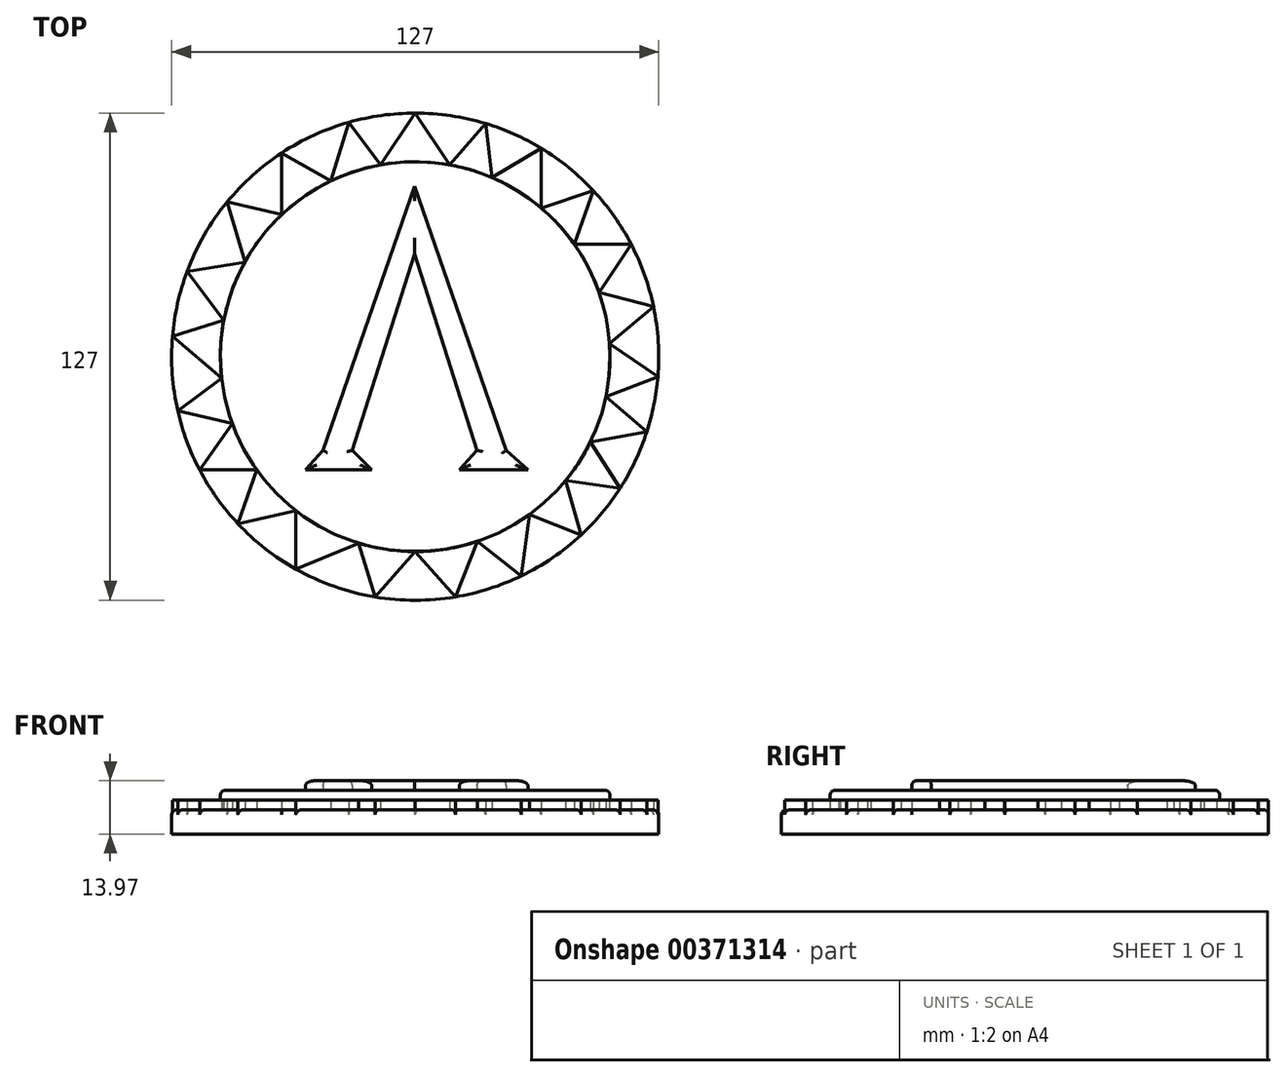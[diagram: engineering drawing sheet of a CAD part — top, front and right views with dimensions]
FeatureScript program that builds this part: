
annotation { "Feature Type Name" : "Feature", "Feature Type Description" : "" }
export const myFeature = defineFeature(function(context is Context, id is Id, definition is map)
    precondition{}
    {
        {
            var Q0;
            Q0=qCreatedBy(makeId("Top.planeOp"),FACE);
            var sketch = newSketch(context, id + "F0", { "sketchPlane" : qUnion([Q0])});
            skCircle(sketch, "E0", {"center": v(0, 0) * mm, "radius": 50.8 * mm});
            skCircle(sketch, "E1", {"center": v(0, 0) * mm, "radius": 63.5 * mm});
            skPoint(sketch, "E2", {"position": v(9.04, 49.99) * mm});
            skPoint(sketch, "E3", {"position": v(-9.05, 49.99) * mm});
            skLineSegment(sketch, "E4", {"start": v(9.04, 49.99) * mm, "end": v(18.33, 60.8) * mm});
            skLineSegment(sketch, "E5", {"start": v(18.33, 60.8) * mm, "end": v(19.99, 46.7) * mm});
            skLineSegment(sketch, "E6", {"start": v(19.99, 46.7) * mm, "end": v(32.82, 54.36) * mm});
            skLineSegment(sketch, "E7", {"start": v(32.82, 54.36) * mm, "end": v(32.82, 38.78) * mm});
            skLineSegment(sketch, "E8", {"start": v(32.82, 38.78) * mm, "end": v(46.5, 43.25) * mm});
            skLineSegment(sketch, "E9", {"start": v(46.5, 43.25) * mm, "end": v(41.51, 29.28) * mm});
            skLineSegment(sketch, "E10", {"start": v(41.51, 29.28) * mm, "end": v(56.35, 29.28) * mm});
            skLineSegment(sketch, "E11", {"start": v(56.35, 29.28) * mm, "end": v(47.98, 16.7) * mm});
            skLineSegment(sketch, "E12", {"start": v(47.98, 16.7) * mm, "end": v(62.14, 13.06) * mm});
            skLineSegment(sketch, "E13", {"start": v(62.14, 13.06) * mm, "end": v(50.69, 3.39) * mm});
            skLineSegment(sketch, "E14", {"start": v(50.69, 3.39) * mm, "end": v(63.28, -5.26) * mm});
            skLineSegment(sketch, "E15", {"start": v(63.28, -5.26) * mm, "end": v(49.7, -10.49) * mm});
            skLineSegment(sketch, "E16", {"start": v(-9.05, 49.99) * mm, "end": v(-17.31, 61.1) * mm});
            skLineSegment(sketch, "E17", {"start": v(-17.31, 61.1) * mm, "end": v(-22.05, 45.77) * mm});
            skLineSegment(sketch, "E18", {"start": v(-22.05, 45.77) * mm, "end": v(-34.79, 53.12) * mm});
            skLineSegment(sketch, "E19", {"start": v(0, 63.5) * mm, "end": v(-9.05, 49.99) * mm});
            skLineSegment(sketch, "E20", {"start": v(0, 63.5) * mm, "end": v(9.04, 49.99) * mm});
            skLineSegment(sketch, "E21", {"start": v(-34.79, 53.12) * mm, "end": v(-34.79, 37.02) * mm});
            skLineSegment(sketch, "E22", {"start": v(-34.79, 37.02) * mm, "end": v(-49.02, 40.36) * mm});
            skLineSegment(sketch, "E23", {"start": v(-49.02, 40.36) * mm, "end": v(-44.42, 24.65) * mm});
            skLineSegment(sketch, "E24", {"start": v(-44.42, 24.65) * mm, "end": v(-59.47, 22.26) * mm});
            skLineSegment(sketch, "E25", {"start": v(-59.47, 22.26) * mm, "end": v(-49.9, 9.5) * mm});
            skLineSegment(sketch, "E26", {"start": v(-49.9, 9.5) * mm, "end": v(-63.28, 5.27) * mm});
            skLineSegment(sketch, "E27", {"start": v(-63.28, 5.27) * mm, "end": v(-50.49, -5.64) * mm});
            skLineSegment(sketch, "E28", {"start": v(-50.49, -5.64) * mm, "end": v(-61.91, -14.1) * mm});
            skLineSegment(sketch, "E29", {"start": v(-61.91, -14.1) * mm, "end": v(-47.71, -17.44) * mm});
            skLineSegment(sketch, "E30", {"start": v(-47.71, -17.44) * mm, "end": v(-56.21, -29.54) * mm});
            skLineSegment(sketch, "E31", {"start": v(-56.21, -29.54) * mm, "end": v(-41.33, -29.54) * mm});
            skLineSegment(sketch, "E32", {"start": v(-41.33, -29.54) * mm, "end": v(-46.22, -43.55) * mm});
            skLineSegment(sketch, "E33", {"start": v(-46.22, -43.55) * mm, "end": v(-31.1, -40.17) * mm});
            skLineSegment(sketch, "E34", {"start": v(-31.1, -40.17) * mm, "end": v(-31.1, -55.36) * mm});
            skLineSegment(sketch, "E35", {"start": v(-31.1, -55.36) * mm, "end": v(-14.78, -48.6) * mm});
            skLineSegment(sketch, "E36", {"start": v(-14.78, -48.6) * mm, "end": v(-10.47, -62.63) * mm});
            skLineSegment(sketch, "E37", {"start": v(-10.47, -62.63) * mm, "end": v(0, -50.8) * mm});
            skLineSegment(sketch, "E38", {"start": v(0, -50.8) * mm, "end": v(10.47, -62.63) * mm});
            skLineSegment(sketch, "E39", {"start": v(10.47, -62.63) * mm, "end": v(16.28, -48.12) * mm});
            skLineSegment(sketch, "E40", {"start": v(16.28, -48.12) * mm, "end": v(27.67, -57.15) * mm});
            skLineSegment(sketch, "E41", {"start": v(27.67, -57.15) * mm, "end": v(29.84, -41.1) * mm});
            skLineSegment(sketch, "E42", {"start": v(29.84, -41.1) * mm, "end": v(43.26, -46.48) * mm});
            skLineSegment(sketch, "E43", {"start": v(43.26, -46.48) * mm, "end": v(39.22, -32.29) * mm});
            skLineSegment(sketch, "E44", {"start": v(39.22, -32.29) * mm, "end": v(53.46, -34.27) * mm});
            skLineSegment(sketch, "E45", {"start": v(53.46, -34.27) * mm, "end": v(45.69, -22.2) * mm});
            skLineSegment(sketch, "E46", {"start": v(49.7, -10.49) * mm, "end": v(60.42, -19.54) * mm});
            skLineSegment(sketch, "E47", {"start": v(45.69, -22.2) * mm, "end": v(60.42, -19.54) * mm});
            skPoint(sketch, "E48", {"position": v(0, 43.48) * mm});
            skPoint(sketch, "E49", {"position": v(0, -25.4) * mm});
            skPoint(sketch, "E50", {"position": v(0, 25.83) * mm});
            skLineSegment(sketch, "E51", {"start": v(0, 25.83) * mm, "end": v(16.25, -25.4) * mm});
            skLineSegment(sketch, "E52", {"start": v(0, 25.83) * mm, "end": v(-16.25, -25.4) * mm});
            skLineSegment(sketch, "E53", {"start": v(0, 43.48) * mm, "end": v(-23.87, -25.4) * mm});
            skLineSegment(sketch, "E54", {"start": v(0, 43.48) * mm, "end": v(23.87, -25.4) * mm});
            skPoint(sketch, "E55", {"position": v(0, -30.48) * mm});
            skLineSegment(sketch, "E56", {"start": v(-23.87, -25.4) * mm, "end": v(-28.47, -30.48) * mm});
            skLineSegment(sketch, "E57", {"start": v(-16.25, -25.4) * mm, "end": v(-11.25, -30.48) * mm});
            skLineSegment(sketch, "E58", {"start": v(16.25, -25.4) * mm, "end": v(11.66, -30.48) * mm});
            skLineSegment(sketch, "E59", {"start": v(23.87, -25.4) * mm, "end": v(29.5, -30.48) * mm});
            skLineSegment(sketch, "E60", {"start": v(-11.25, -30.48) * mm, "end": v(-28.47, -30.48) * mm});
            skLineSegment(sketch, "E61", {"start": v(11.66, -30.48) * mm, "end": v(29.5, -30.48) * mm});
            skPoint(sketch, "E62", {"position": v(0, 50.8) * mm});
            skLineSegment(sketch, "E63", {"start": v(0, 0) * mm, "end": v(-8.2, 0) * mm});
            skLineSegment(sketch, "E64", {"start": v(0, 0) * mm, "end": v(8.2, 0) * mm});
            skSolve(sketch);
        }
        {
            var Q0;
            Q0 = qSketchRegion(id + "F0", true);
            var Q1;
            Q1=makeQuery(id+"F0.imprint","IMPRINT",FACE,{"disambiguationData":[TD([[makeQuery(id+"F0.imprint","IMPRINT",EDGE,{"derivedFrom":sQuery(id+"F0.wireOp",EDGE,"E51")}),-1.0]])]});
            var Q2;
            Q2=makeQuery(id+"F0.imprint","IMPRINT",FACE,{"disambiguationData":[TD([[makeQuery(id+"F0.imprint","IMPRINT",EDGE,{"derivedFrom":sQuery(id+"F0.wireOp",EDGE,"E51")}),1.0]])]});
            var Q3;
            Q3=makeQuery(id+"F0.imprint","IMPRINT",FACE,{"disambiguationData":[TD([[makeQuery(id+"F0.imprint","IMPRINT",EDGE,{"derivedFrom":sQuery(id+"F0.wireOp",EDGE,"E53")}),-1.0]])]});
            extrude(context, id + "F1", {"entities" : qUnion([Q0, Q1, Q2, Q3]), "depth" : 6.35 * mm});
        }
        {
            var Q0;
            Q0=makeQuery(id+"F1.opExtrude","CAP_FACE",FACE,{"disambiguationData":[OSD([sQuery(id+"F0.wireOp",EDGE,"E0"),sQuery(id+"F0.wireOp",EDGE,"E1")])],"isStart":false});
            var sketch = newSketch(context, id + "F2", { "sketchPlane" : qUnion([Q0])});
            skCircle(sketch, "E65", {"center": v(0, 0) * mm, "radius": 63.5 * mm});
            skPoint(sketch, "E66", {"position": v(9.04, 49.99) * mm});
            skPoint(sketch, "E67", {"position": v(-9.05, 49.99) * mm});
            skLineSegment(sketch, "E68", {"start": v(9.04, 49.99) * mm, "end": v(18.33, 60.8) * mm});
            skLineSegment(sketch, "E69", {"start": v(18.33, 60.8) * mm, "end": v(19.99, 46.7) * mm});
            skLineSegment(sketch, "E70", {"start": v(19.99, 46.7) * mm, "end": v(32.82, 54.36) * mm});
            skLineSegment(sketch, "E71", {"start": v(32.82, 54.36) * mm, "end": v(32.82, 38.78) * mm});
            skLineSegment(sketch, "E72", {"start": v(32.82, 38.78) * mm, "end": v(46.5, 43.25) * mm});
            skLineSegment(sketch, "E73", {"start": v(46.5, 43.25) * mm, "end": v(41.51, 29.28) * mm});
            skLineSegment(sketch, "E74", {"start": v(41.51, 29.28) * mm, "end": v(56.35, 29.28) * mm});
            skLineSegment(sketch, "E75", {"start": v(56.35, 29.28) * mm, "end": v(47.98, 16.7) * mm});
            skLineSegment(sketch, "E76", {"start": v(47.98, 16.7) * mm, "end": v(62.14, 13.06) * mm});
            skLineSegment(sketch, "E77", {"start": v(62.14, 13.06) * mm, "end": v(50.69, 3.39) * mm});
            skLineSegment(sketch, "E78", {"start": v(50.69, 3.39) * mm, "end": v(63.28, -5.26) * mm});
            skLineSegment(sketch, "E79", {"start": v(63.28, -5.26) * mm, "end": v(49.7, -10.49) * mm});
            skLineSegment(sketch, "E80", {"start": v(-9.05, 49.99) * mm, "end": v(-17.31, 61.1) * mm});
            skLineSegment(sketch, "E81", {"start": v(-17.31, 61.1) * mm, "end": v(-22.05, 45.77) * mm});
            skLineSegment(sketch, "E82", {"start": v(-22.05, 45.77) * mm, "end": v(-34.79, 53.12) * mm});
            skLineSegment(sketch, "E83", {"start": v(0, 63.5) * mm, "end": v(-9.05, 49.99) * mm});
            skLineSegment(sketch, "E84", {"start": v(0, 63.5) * mm, "end": v(9.04, 49.99) * mm});
            skLineSegment(sketch, "E85", {"start": v(-34.79, 53.12) * mm, "end": v(-34.79, 37.02) * mm});
            skLineSegment(sketch, "E86", {"start": v(-34.79, 37.02) * mm, "end": v(-49.02, 40.36) * mm});
            skLineSegment(sketch, "E87", {"start": v(-49.02, 40.36) * mm, "end": v(-44.42, 24.65) * mm});
            skLineSegment(sketch, "E88", {"start": v(-44.42, 24.65) * mm, "end": v(-59.47, 22.26) * mm});
            skLineSegment(sketch, "E89", {"start": v(-59.47, 22.26) * mm, "end": v(-49.9, 9.5) * mm});
            skLineSegment(sketch, "E90", {"start": v(-49.9, 9.5) * mm, "end": v(-63.28, 5.27) * mm});
            skLineSegment(sketch, "E91", {"start": v(-63.28, 5.27) * mm, "end": v(-50.49, -5.64) * mm});
            skLineSegment(sketch, "E92", {"start": v(-50.49, -5.64) * mm, "end": v(-61.91, -14.1) * mm});
            skLineSegment(sketch, "E93", {"start": v(-61.91, -14.1) * mm, "end": v(-47.71, -17.44) * mm});
            skLineSegment(sketch, "E94", {"start": v(-47.71, -17.44) * mm, "end": v(-56.21, -29.54) * mm});
            skLineSegment(sketch, "E95", {"start": v(-56.21, -29.54) * mm, "end": v(-41.33, -29.54) * mm});
            skLineSegment(sketch, "E96", {"start": v(-41.33, -29.54) * mm, "end": v(-46.22, -43.55) * mm});
            skLineSegment(sketch, "E97", {"start": v(-46.22, -43.55) * mm, "end": v(-31.1, -40.17) * mm});
            skLineSegment(sketch, "E98", {"start": v(-31.1, -40.17) * mm, "end": v(-31.1, -55.36) * mm});
            skLineSegment(sketch, "E99", {"start": v(-31.1, -55.36) * mm, "end": v(-14.78, -48.6) * mm});
            skLineSegment(sketch, "E100", {"start": v(-14.78, -48.6) * mm, "end": v(-10.47, -62.63) * mm});
            skLineSegment(sketch, "E101", {"start": v(-10.47, -62.63) * mm, "end": v(0, -50.8) * mm});
            skLineSegment(sketch, "E102", {"start": v(0, -50.8) * mm, "end": v(10.47, -62.63) * mm});
            skLineSegment(sketch, "E103", {"start": v(10.47, -62.63) * mm, "end": v(16.28, -48.12) * mm});
            skLineSegment(sketch, "E104", {"start": v(16.28, -48.12) * mm, "end": v(27.67, -57.15) * mm});
            skLineSegment(sketch, "E105", {"start": v(27.67, -57.15) * mm, "end": v(29.84, -41.1) * mm});
            skLineSegment(sketch, "E106", {"start": v(29.84, -41.1) * mm, "end": v(43.26, -46.48) * mm});
            skLineSegment(sketch, "E107", {"start": v(43.26, -46.48) * mm, "end": v(39.22, -32.29) * mm});
            skLineSegment(sketch, "E108", {"start": v(39.22, -32.29) * mm, "end": v(53.46, -34.27) * mm});
            skLineSegment(sketch, "E109", {"start": v(53.46, -34.27) * mm, "end": v(45.69, -22.2) * mm});
            skLineSegment(sketch, "E110", {"start": v(49.7, -10.49) * mm, "end": v(60.42, -19.54) * mm});
            skLineSegment(sketch, "E111", {"start": v(45.69, -22.2) * mm, "end": v(60.42, -19.54) * mm});
            skPoint(sketch, "E112", {"position": v(-74.35, 61.13) * mm});
            skPoint(sketch, "E113", {"position": v(-74.35, -7.75) * mm});
            skPoint(sketch, "E114", {"position": v(-74.35, 43.48) * mm});
            skPoint(sketch, "E115", {"position": v(-74.35, -12.83) * mm});
            skSolve(sketch);
        }
        {
            var Q0;
            Q0=makeQuery(id+"F2.imprint","IMPRINT",FACE,{"disambiguationData":[TD([[makeQuery(id+"F2.imprint","IMPRINT",EDGE,{"derivedFrom":sQuery(id+"F2.wireOp",EDGE,"E68")}),-1.0]])]});
            extrude(context, id + "F3", {"entities" : qUnion([Q0]), "operationType" : NewBodyOperationType.ADD, "depth" : 2.54 * mm});
        }
        {
            var Q0;
            Q0=makeQuery(id+"F3.opExtrude","CAP_FACE",FACE,{"disambiguationData":[OSD([sQuery(id+"F2.wireOp",EDGE,"E68"),sQuery(id+"F2.wireOp",EDGE,"E69"),sQuery(id+"F2.wireOp",EDGE,"E70"),sQuery(id+"F2.wireOp",EDGE,"E71"),sQuery(id+"F2.wireOp",EDGE,"E72"),sQuery(id+"F2.wireOp",EDGE,"E73"),sQuery(id+"F2.wireOp",EDGE,"E74"),sQuery(id+"F2.wireOp",EDGE,"E75"),sQuery(id+"F2.wireOp",EDGE,"E76"),sQuery(id+"F2.wireOp",EDGE,"E77"),sQuery(id+"F2.wireOp",EDGE,"E78"),sQuery(id+"F2.wireOp",EDGE,"E79"),sQuery(id+"F2.wireOp",EDGE,"E80"),sQuery(id+"F2.wireOp",EDGE,"E81"),sQuery(id+"F2.wireOp",EDGE,"E82"),sQuery(id+"F2.wireOp",EDGE,"E83"),sQuery(id+"F2.wireOp",EDGE,"E84"),sQuery(id+"F2.wireOp",EDGE,"E85"),sQuery(id+"F2.wireOp",EDGE,"E86"),sQuery(id+"F2.wireOp",EDGE,"E87"),sQuery(id+"F2.wireOp",EDGE,"E88"),sQuery(id+"F2.wireOp",EDGE,"E89"),sQuery(id+"F2.wireOp",EDGE,"E90"),sQuery(id+"F2.wireOp",EDGE,"E91"),sQuery(id+"F2.wireOp",EDGE,"E92"),sQuery(id+"F2.wireOp",EDGE,"E93"),sQuery(id+"F2.wireOp",EDGE,"E94"),sQuery(id+"F2.wireOp",EDGE,"E95"),sQuery(id+"F2.wireOp",EDGE,"E96"),sQuery(id+"F2.wireOp",EDGE,"E97"),sQuery(id+"F2.wireOp",EDGE,"E98"),sQuery(id+"F2.wireOp",EDGE,"E99"),sQuery(id+"F2.wireOp",EDGE,"E100"),sQuery(id+"F2.wireOp",EDGE,"E101"),sQuery(id+"F2.wireOp",EDGE,"E102"),sQuery(id+"F2.wireOp",EDGE,"E103"),sQuery(id+"F2.wireOp",EDGE,"E104"),sQuery(id+"F2.wireOp",EDGE,"E105"),sQuery(id+"F2.wireOp",EDGE,"E106"),sQuery(id+"F2.wireOp",EDGE,"E107"),sQuery(id+"F2.wireOp",EDGE,"E108"),sQuery(id+"F2.wireOp",EDGE,"E109"),sQuery(id+"F2.wireOp",EDGE,"E110"),sQuery(id+"F2.wireOp",EDGE,"E111")])],"isStart":false});
            var sketch = newSketch(context, id + "F4", { "sketchPlane" : qUnion([Q0])});
            skPoint(sketch, "E116", {"position": v(0, 0) * mm});
            skCircle(sketch, "E117", {"center": v(0, 0) * mm, "radius": 50.8 * mm});
            skPoint(sketch, "E118", {"position": v(-0.12, 44.46) * mm});
            skPoint(sketch, "E119", {"position": v(-0.12, 26.8) * mm});
            skLineSegment(sketch, "E120", {"start": v(-0.12, 26.8) * mm, "end": v(16.14, -24.42) * mm});
            skLineSegment(sketch, "E121", {"start": v(-0.12, 26.8) * mm, "end": v(-16.37, -24.42) * mm});
            skLineSegment(sketch, "E122", {"start": v(-0.12, 44.46) * mm, "end": v(-24, -24.42) * mm});
            skLineSegment(sketch, "E123", {"start": v(-0.12, 44.46) * mm, "end": v(23.76, -24.42) * mm});
            skLineSegment(sketch, "E124", {"start": v(-24, -24.42) * mm, "end": v(-28.59, -29.5) * mm});
            skLineSegment(sketch, "E125", {"start": v(-16.37, -24.42) * mm, "end": v(-11.37, -29.5) * mm});
            skLineSegment(sketch, "E126", {"start": v(16.14, -24.42) * mm, "end": v(11.54, -29.5) * mm});
            skLineSegment(sketch, "E127", {"start": v(23.76, -24.42) * mm, "end": v(29.37, -29.5) * mm});
            skLineSegment(sketch, "E128", {"start": v(-11.37, -29.5) * mm, "end": v(-28.59, -29.5) * mm});
            skLineSegment(sketch, "E129", {"start": v(11.54, -29.5) * mm, "end": v(29.37, -29.5) * mm});
            skSolve(sketch);
        }
        {
            var Q0;
            Q0=makeQuery(id+"F4.imprint","IMPRINT",FACE,{"disambiguationData":[TD([[makeQuery(id+"F4.imprint","IMPRINT",EDGE,{"derivedFrom":sQuery(id+"F4.wireOp",EDGE,"E120")}),-1.0]])]});
            extrude(context, id + "F5", {"entities" : qUnion([Q0]), "operationType" : NewBodyOperationType.ADD, "depth" : 2.54 * mm});
        }
        {
            var Q0;
            Q0=makeQuery(id+"F5.boolean.opBoolean","SPLIT",FACE,{"disambiguationData":[TD([makeQuery(id+"F5.opExtrude","SWEPT_FACE",FACE,{"disambiguationData":[OSD([sQuery(id+"F4.wireOp",EDGE,"E120")])]}),makeQuery(id+"F5.opExtrude","SWEPT_FACE",FACE,{"disambiguationData":[OSD([sQuery(id+"F4.wireOp",EDGE,"E121")])]}),makeQuery(id+"F5.opExtrude","SWEPT_FACE",FACE,{"disambiguationData":[OSD([sQuery(id+"F4.wireOp",EDGE,"E122")])]}),makeQuery(id+"F5.opExtrude","SWEPT_FACE",FACE,{"disambiguationData":[OSD([sQuery(id+"F4.wireOp",EDGE,"E123")])]}),makeQuery(id+"F5.opExtrude","SWEPT_FACE",FACE,{"disambiguationData":[OSD([sQuery(id+"F4.wireOp",EDGE,"E124")])]}),makeQuery(id+"F5.opExtrude","SWEPT_FACE",FACE,{"disambiguationData":[OSD([sQuery(id+"F4.wireOp",EDGE,"E125")])]}),makeQuery(id+"F5.opExtrude","SWEPT_FACE",FACE,{"disambiguationData":[OSD([sQuery(id+"F4.wireOp",EDGE,"E126")])]}),makeQuery(id+"F5.opExtrude","SWEPT_FACE",FACE,{"disambiguationData":[OSD([sQuery(id+"F4.wireOp",EDGE,"E127")])]}),makeQuery(id+"F5.opExtrude","SWEPT_FACE",FACE,{"disambiguationData":[OSD([sQuery(id+"F4.wireOp",EDGE,"E128")])]}),makeQuery(id+"F5.opExtrude","SWEPT_FACE",FACE,{"disambiguationData":[OSD([sQuery(id+"F4.wireOp",EDGE,"E129")])]})])],"derivedFrom":makeQuery(id+"F3.opExtrude","CAP_FACE",FACE,{"disambiguationData":[OSD([sQuery(id+"F2.wireOp",EDGE,"E68"),sQuery(id+"F2.wireOp",EDGE,"E69"),sQuery(id+"F2.wireOp",EDGE,"E70"),sQuery(id+"F2.wireOp",EDGE,"E71"),sQuery(id+"F2.wireOp",EDGE,"E72"),sQuery(id+"F2.wireOp",EDGE,"E73"),sQuery(id+"F2.wireOp",EDGE,"E74"),sQuery(id+"F2.wireOp",EDGE,"E75"),sQuery(id+"F2.wireOp",EDGE,"E76"),sQuery(id+"F2.wireOp",EDGE,"E77"),sQuery(id+"F2.wireOp",EDGE,"E78"),sQuery(id+"F2.wireOp",EDGE,"E79"),sQuery(id+"F2.wireOp",EDGE,"E80"),sQuery(id+"F2.wireOp",EDGE,"E81"),sQuery(id+"F2.wireOp",EDGE,"E82"),sQuery(id+"F2.wireOp",EDGE,"E83"),sQuery(id+"F2.wireOp",EDGE,"E84"),sQuery(id+"F2.wireOp",EDGE,"E85"),sQuery(id+"F2.wireOp",EDGE,"E86"),sQuery(id+"F2.wireOp",EDGE,"E87"),sQuery(id+"F2.wireOp",EDGE,"E88"),sQuery(id+"F2.wireOp",EDGE,"E89"),sQuery(id+"F2.wireOp",EDGE,"E90"),sQuery(id+"F2.wireOp",EDGE,"E91"),sQuery(id+"F2.wireOp",EDGE,"E92"),sQuery(id+"F2.wireOp",EDGE,"E93"),sQuery(id+"F2.wireOp",EDGE,"E94"),sQuery(id+"F2.wireOp",EDGE,"E95"),sQuery(id+"F2.wireOp",EDGE,"E96"),sQuery(id+"F2.wireOp",EDGE,"E97"),sQuery(id+"F2.wireOp",EDGE,"E98"),sQuery(id+"F2.wireOp",EDGE,"E99"),sQuery(id+"F2.wireOp",EDGE,"E100"),sQuery(id+"F2.wireOp",EDGE,"E101"),sQuery(id+"F2.wireOp",EDGE,"E102"),sQuery(id+"F2.wireOp",EDGE,"E103"),sQuery(id+"F2.wireOp",EDGE,"E104"),sQuery(id+"F2.wireOp",EDGE,"E105"),sQuery(id+"F2.wireOp",EDGE,"E106"),sQuery(id+"F2.wireOp",EDGE,"E107"),sQuery(id+"F2.wireOp",EDGE,"E108"),sQuery(id+"F2.wireOp",EDGE,"E109"),sQuery(id+"F2.wireOp",EDGE,"E110"),sQuery(id+"F2.wireOp",EDGE,"E111")])],"isStart":false})});
            extrude(context, id + "F6", {"entities" : qUnion([Q0]), "operationType" : NewBodyOperationType.ADD, "depth" : 5.08 * mm});
        }
        {
            var Q0;
            Q0=makeQuery(id+"F6.opExtrude","CAP_EDGE",EDGE,{"disambiguationData":[OSD([sQuery(id+"F4.wireOp",EDGE,"E122")])],"isStart":false});
            var Q1;
            Q1=makeQuery(id+"F6.opExtrude","CAP_EDGE",EDGE,{"disambiguationData":[OSD([sQuery(id+"F4.wireOp",EDGE,"E121")])],"isStart":false});
            var Q2;
            Q2=makeQuery(id+"F6.opExtrude","CAP_EDGE",EDGE,{"disambiguationData":[OSD([sQuery(id+"F4.wireOp",EDGE,"E125")])],"isStart":false});
            var Q3;
            Q3=makeQuery(id+"F6.opExtrude","CAP_EDGE",EDGE,{"disambiguationData":[OSD([sQuery(id+"F4.wireOp",EDGE,"E128")])],"isStart":false});
            var Q4;
            Q4=makeQuery(id+"F6.opExtrude","CAP_EDGE",EDGE,{"disambiguationData":[OSD([sQuery(id+"F4.wireOp",EDGE,"E124")])],"isStart":false});
            var Q5;
            Q5=makeQuery(id+"F6.opExtrude","CAP_EDGE",EDGE,{"disambiguationData":[OSD([sQuery(id+"F4.wireOp",EDGE,"E126")])],"isStart":false});
            var Q6;
            Q6=makeQuery(id+"F6.opExtrude","CAP_EDGE",EDGE,{"disambiguationData":[OSD([sQuery(id+"F4.wireOp",EDGE,"E129")])],"isStart":false});
            var Q7;
            Q7=makeQuery(id+"F6.opExtrude","CAP_EDGE",EDGE,{"disambiguationData":[OSD([sQuery(id+"F4.wireOp",EDGE,"E127")])],"isStart":false});
            var Q8;
            Q8=makeQuery(id+"F6.opExtrude","CAP_EDGE",EDGE,{"disambiguationData":[OSD([sQuery(id+"F4.wireOp",EDGE,"E123")])],"isStart":false});
            var Q9;
            Q9=makeQuery(id+"F6.opExtrude","CAP_EDGE",EDGE,{"disambiguationData":[OSD([sQuery(id+"F4.wireOp",EDGE,"E120")])],"isStart":false});
            fillet(context, id + "F7", {"entities" : qUnion([Q0, Q1, Q2, Q3, Q4, Q5, Q6, Q7, Q8, Q9]), "radius" : 1.27 * mm, "tangentPropagation" : true, "allowEdgeOverflow" : false});
        }
        {
            var Q0;
            {var subQ0=sQuery(id+"F0.wireOp",EDGE,"E1");Q0=makeQuery(id+"F3.boolean.opBoolean","SPLIT",EDGE,{"disambiguationData":[TD([makeQuery(id+"F1.opExtrude","SWEPT_FACE",FACE,{"disambiguationData":[OSD([subQ0])]}),makeQuery(id+"F1.opExtrude","CAP_FACE",FACE,{"disambiguationData":[OSD([subQ0])],"isStart":false}),makeQuery(id+"F3.opExtrude","SWEPT_FACE",FACE,{"disambiguationData":[OSD([sQuery(id+"F2.wireOp",EDGE,"E82")])]}),makeQuery(id+"F3.opExtrude","SWEPT_FACE",FACE,{"disambiguationData":[OSD([sQuery(id+"F2.wireOp",EDGE,"E85")])]}),makeQuery(id+"F3.opExtrude","SWEPT_FACE",FACE,{"disambiguationData":[OSD([sQuery(id+"F2.wireOp",EDGE,"E86")])]}),makeQuery(id+"F3.opExtrude","SWEPT_FACE",FACE,{"disambiguationData":[OSD([sQuery(id+"F2.wireOp",EDGE,"E87")])]})])],"derivedFrom":makeQuery(id+"F1.opExtrude","CAP_EDGE",EDGE,{"disambiguationData":[OSD([subQ0])],"isStart":false})});}
            var Q1;
            {var subQ0=sQuery(id+"F0.wireOp",EDGE,"E1");Q1=makeQuery(id+"F3.boolean.opBoolean","SPLIT",EDGE,{"disambiguationData":[TD([makeQuery(id+"F1.opExtrude","SWEPT_FACE",FACE,{"disambiguationData":[OSD([subQ0])]}),makeQuery(id+"F1.opExtrude","CAP_FACE",FACE,{"disambiguationData":[OSD([subQ0])],"isStart":false}),makeQuery(id+"F3.opExtrude","SWEPT_FACE",FACE,{"disambiguationData":[OSD([sQuery(id+"F2.wireOp",EDGE,"E80")])]}),makeQuery(id+"F3.opExtrude","SWEPT_FACE",FACE,{"disambiguationData":[OSD([sQuery(id+"F2.wireOp",EDGE,"E81")])]}),makeQuery(id+"F3.opExtrude","SWEPT_FACE",FACE,{"disambiguationData":[OSD([sQuery(id+"F2.wireOp",EDGE,"E82")])]}),makeQuery(id+"F3.opExtrude","SWEPT_FACE",FACE,{"disambiguationData":[OSD([sQuery(id+"F2.wireOp",EDGE,"E85")])]})])],"derivedFrom":makeQuery(id+"F1.opExtrude","CAP_EDGE",EDGE,{"disambiguationData":[OSD([subQ0])],"isStart":false})});}
            var Q2;
            {var subQ0=sQuery(id+"F0.wireOp",EDGE,"E1");Q2=makeQuery(id+"F3.boolean.opBoolean","SPLIT",EDGE,{"disambiguationData":[TD([makeQuery(id+"F1.opExtrude","SWEPT_FACE",FACE,{"disambiguationData":[OSD([subQ0])]}),makeQuery(id+"F1.opExtrude","CAP_FACE",FACE,{"disambiguationData":[OSD([subQ0])],"isStart":false}),makeQuery(id+"F3.opExtrude","SWEPT_FACE",FACE,{"disambiguationData":[OSD([sQuery(id+"F2.wireOp",EDGE,"E80")])]}),makeQuery(id+"F3.opExtrude","SWEPT_FACE",FACE,{"disambiguationData":[OSD([sQuery(id+"F2.wireOp",EDGE,"E81")])]}),makeQuery(id+"F3.opExtrude","SWEPT_FACE",FACE,{"disambiguationData":[OSD([sQuery(id+"F2.wireOp",EDGE,"E83")])]}),makeQuery(id+"F3.opExtrude","SWEPT_FACE",FACE,{"disambiguationData":[OSD([sQuery(id+"F2.wireOp",EDGE,"E84")])]})])],"derivedFrom":makeQuery(id+"F1.opExtrude","CAP_EDGE",EDGE,{"disambiguationData":[OSD([subQ0])],"isStart":false})});}
            var Q3;
            {var subQ0=sQuery(id+"F0.wireOp",EDGE,"E1");Q3=makeQuery(id+"F3.boolean.opBoolean","SPLIT",EDGE,{"disambiguationData":[TD([makeQuery(id+"F1.opExtrude","SWEPT_FACE",FACE,{"disambiguationData":[OSD([subQ0])]}),makeQuery(id+"F1.opExtrude","CAP_FACE",FACE,{"disambiguationData":[OSD([subQ0])],"isStart":false}),makeQuery(id+"F3.opExtrude","SWEPT_FACE",FACE,{"disambiguationData":[OSD([sQuery(id+"F2.wireOp",EDGE,"E68")])]}),makeQuery(id+"F3.opExtrude","SWEPT_FACE",FACE,{"disambiguationData":[OSD([sQuery(id+"F2.wireOp",EDGE,"E69")])]}),makeQuery(id+"F3.opExtrude","SWEPT_FACE",FACE,{"disambiguationData":[OSD([sQuery(id+"F2.wireOp",EDGE,"E83")])]}),makeQuery(id+"F3.opExtrude","SWEPT_FACE",FACE,{"disambiguationData":[OSD([sQuery(id+"F2.wireOp",EDGE,"E84")])]})])],"derivedFrom":makeQuery(id+"F1.opExtrude","CAP_EDGE",EDGE,{"disambiguationData":[OSD([subQ0])],"isStart":false})});}
            var Q4;
            {var subQ0=sQuery(id+"F0.wireOp",EDGE,"E1");Q4=makeQuery(id+"F3.boolean.opBoolean","SPLIT",EDGE,{"disambiguationData":[TD([makeQuery(id+"F1.opExtrude","SWEPT_FACE",FACE,{"disambiguationData":[OSD([subQ0])]}),makeQuery(id+"F1.opExtrude","CAP_FACE",FACE,{"disambiguationData":[OSD([subQ0])],"isStart":false}),makeQuery(id+"F3.opExtrude","SWEPT_FACE",FACE,{"disambiguationData":[OSD([sQuery(id+"F2.wireOp",EDGE,"E68")])]}),makeQuery(id+"F3.opExtrude","SWEPT_FACE",FACE,{"disambiguationData":[OSD([sQuery(id+"F2.wireOp",EDGE,"E69")])]}),makeQuery(id+"F3.opExtrude","SWEPT_FACE",FACE,{"disambiguationData":[OSD([sQuery(id+"F2.wireOp",EDGE,"E70")])]}),makeQuery(id+"F3.opExtrude","SWEPT_FACE",FACE,{"disambiguationData":[OSD([sQuery(id+"F2.wireOp",EDGE,"E71")])]})])],"derivedFrom":makeQuery(id+"F1.opExtrude","CAP_EDGE",EDGE,{"disambiguationData":[OSD([subQ0])],"isStart":false})});}
            var Q5;
            {var subQ0=sQuery(id+"F0.wireOp",EDGE,"E1");Q5=makeQuery(id+"F3.boolean.opBoolean","SPLIT",EDGE,{"disambiguationData":[TD([makeQuery(id+"F1.opExtrude","SWEPT_FACE",FACE,{"disambiguationData":[OSD([subQ0])]}),makeQuery(id+"F1.opExtrude","CAP_FACE",FACE,{"disambiguationData":[OSD([subQ0])],"isStart":false}),makeQuery(id+"F3.opExtrude","SWEPT_FACE",FACE,{"disambiguationData":[OSD([sQuery(id+"F2.wireOp",EDGE,"E70")])]}),makeQuery(id+"F3.opExtrude","SWEPT_FACE",FACE,{"disambiguationData":[OSD([sQuery(id+"F2.wireOp",EDGE,"E71")])]}),makeQuery(id+"F3.opExtrude","SWEPT_FACE",FACE,{"disambiguationData":[OSD([sQuery(id+"F2.wireOp",EDGE,"E72")])]}),makeQuery(id+"F3.opExtrude","SWEPT_FACE",FACE,{"disambiguationData":[OSD([sQuery(id+"F2.wireOp",EDGE,"E73")])]})])],"derivedFrom":makeQuery(id+"F1.opExtrude","CAP_EDGE",EDGE,{"disambiguationData":[OSD([subQ0])],"isStart":false})});}
            var Q6;
            {var subQ0=sQuery(id+"F0.wireOp",EDGE,"E1");Q6=makeQuery(id+"F3.boolean.opBoolean","SPLIT",EDGE,{"disambiguationData":[TD([makeQuery(id+"F1.opExtrude","SWEPT_FACE",FACE,{"disambiguationData":[OSD([subQ0])]}),makeQuery(id+"F1.opExtrude","CAP_FACE",FACE,{"disambiguationData":[OSD([subQ0])],"isStart":false}),makeQuery(id+"F3.opExtrude","SWEPT_FACE",FACE,{"disambiguationData":[OSD([sQuery(id+"F2.wireOp",EDGE,"E72")])]}),makeQuery(id+"F3.opExtrude","SWEPT_FACE",FACE,{"disambiguationData":[OSD([sQuery(id+"F2.wireOp",EDGE,"E73")])]}),makeQuery(id+"F3.opExtrude","SWEPT_FACE",FACE,{"disambiguationData":[OSD([sQuery(id+"F2.wireOp",EDGE,"E74")])]}),makeQuery(id+"F3.opExtrude","SWEPT_FACE",FACE,{"disambiguationData":[OSD([sQuery(id+"F2.wireOp",EDGE,"E75")])]})])],"derivedFrom":makeQuery(id+"F1.opExtrude","CAP_EDGE",EDGE,{"disambiguationData":[OSD([subQ0])],"isStart":false})});}
            var Q7;
            {var subQ0=sQuery(id+"F0.wireOp",EDGE,"E1");Q7=makeQuery(id+"F3.boolean.opBoolean","SPLIT",EDGE,{"disambiguationData":[TD([makeQuery(id+"F1.opExtrude","SWEPT_FACE",FACE,{"disambiguationData":[OSD([subQ0])]}),makeQuery(id+"F1.opExtrude","CAP_FACE",FACE,{"disambiguationData":[OSD([subQ0])],"isStart":false}),makeQuery(id+"F3.opExtrude","SWEPT_FACE",FACE,{"disambiguationData":[OSD([sQuery(id+"F2.wireOp",EDGE,"E74")])]}),makeQuery(id+"F3.opExtrude","SWEPT_FACE",FACE,{"disambiguationData":[OSD([sQuery(id+"F2.wireOp",EDGE,"E75")])]}),makeQuery(id+"F3.opExtrude","SWEPT_FACE",FACE,{"disambiguationData":[OSD([sQuery(id+"F2.wireOp",EDGE,"E76")])]}),makeQuery(id+"F3.opExtrude","SWEPT_FACE",FACE,{"disambiguationData":[OSD([sQuery(id+"F2.wireOp",EDGE,"E77")])]})])],"derivedFrom":makeQuery(id+"F1.opExtrude","CAP_EDGE",EDGE,{"disambiguationData":[OSD([subQ0])],"isStart":false})});}
            var Q8;
            {var subQ0=sQuery(id+"F0.wireOp",EDGE,"E1");Q8=makeQuery(id+"F3.boolean.opBoolean","SPLIT",EDGE,{"disambiguationData":[TD([makeQuery(id+"F1.opExtrude","SWEPT_FACE",FACE,{"disambiguationData":[OSD([subQ0])]}),makeQuery(id+"F1.opExtrude","CAP_FACE",FACE,{"disambiguationData":[OSD([subQ0])],"isStart":false}),makeQuery(id+"F3.opExtrude","SWEPT_FACE",FACE,{"disambiguationData":[OSD([sQuery(id+"F2.wireOp",EDGE,"E76")])]}),makeQuery(id+"F3.opExtrude","SWEPT_FACE",FACE,{"disambiguationData":[OSD([sQuery(id+"F2.wireOp",EDGE,"E77")])]}),makeQuery(id+"F3.opExtrude","SWEPT_FACE",FACE,{"disambiguationData":[OSD([sQuery(id+"F2.wireOp",EDGE,"E78")])]}),makeQuery(id+"F3.opExtrude","SWEPT_FACE",FACE,{"disambiguationData":[OSD([sQuery(id+"F2.wireOp",EDGE,"E79")])]})])],"derivedFrom":makeQuery(id+"F1.opExtrude","CAP_EDGE",EDGE,{"disambiguationData":[OSD([subQ0])],"isStart":false})});}
            var Q9;
            {var subQ0=sQuery(id+"F0.wireOp",EDGE,"E1");Q9=makeQuery(id+"F3.boolean.opBoolean","SPLIT",EDGE,{"disambiguationData":[TD([makeQuery(id+"F1.opExtrude","SWEPT_FACE",FACE,{"disambiguationData":[OSD([subQ0])]}),makeQuery(id+"F1.opExtrude","CAP_FACE",FACE,{"disambiguationData":[OSD([subQ0])],"isStart":false}),makeQuery(id+"F3.opExtrude","SWEPT_FACE",FACE,{"disambiguationData":[OSD([sQuery(id+"F2.wireOp",EDGE,"E78")])]}),makeQuery(id+"F3.opExtrude","SWEPT_FACE",FACE,{"disambiguationData":[OSD([sQuery(id+"F2.wireOp",EDGE,"E79")])]}),makeQuery(id+"F3.opExtrude","SWEPT_FACE",FACE,{"disambiguationData":[OSD([sQuery(id+"F2.wireOp",EDGE,"E110")])]}),makeQuery(id+"F3.opExtrude","SWEPT_FACE",FACE,{"disambiguationData":[OSD([sQuery(id+"F2.wireOp",EDGE,"E111")])]})])],"derivedFrom":makeQuery(id+"F1.opExtrude","CAP_EDGE",EDGE,{"disambiguationData":[OSD([subQ0])],"isStart":false})});}
            var Q10;
            {var subQ0=sQuery(id+"F0.wireOp",EDGE,"E1");Q10=makeQuery(id+"F3.boolean.opBoolean","SPLIT",EDGE,{"disambiguationData":[TD([makeQuery(id+"F1.opExtrude","SWEPT_FACE",FACE,{"disambiguationData":[OSD([subQ0])]}),makeQuery(id+"F1.opExtrude","CAP_FACE",FACE,{"disambiguationData":[OSD([subQ0])],"isStart":false}),makeQuery(id+"F3.opExtrude","SWEPT_FACE",FACE,{"disambiguationData":[OSD([sQuery(id+"F2.wireOp",EDGE,"E108")])]}),makeQuery(id+"F3.opExtrude","SWEPT_FACE",FACE,{"disambiguationData":[OSD([sQuery(id+"F2.wireOp",EDGE,"E109")])]}),makeQuery(id+"F3.opExtrude","SWEPT_FACE",FACE,{"disambiguationData":[OSD([sQuery(id+"F2.wireOp",EDGE,"E110")])]}),makeQuery(id+"F3.opExtrude","SWEPT_FACE",FACE,{"disambiguationData":[OSD([sQuery(id+"F2.wireOp",EDGE,"E111")])]})])],"derivedFrom":makeQuery(id+"F1.opExtrude","CAP_EDGE",EDGE,{"disambiguationData":[OSD([subQ0])],"isStart":false})});}
            var Q11;
            {var subQ0=sQuery(id+"F0.wireOp",EDGE,"E1");Q11=makeQuery(id+"F3.boolean.opBoolean","SPLIT",EDGE,{"disambiguationData":[TD([makeQuery(id+"F1.opExtrude","SWEPT_FACE",FACE,{"disambiguationData":[OSD([subQ0])]}),makeQuery(id+"F1.opExtrude","CAP_FACE",FACE,{"disambiguationData":[OSD([subQ0])],"isStart":false}),makeQuery(id+"F3.opExtrude","SWEPT_FACE",FACE,{"disambiguationData":[OSD([sQuery(id+"F2.wireOp",EDGE,"E106")])]}),makeQuery(id+"F3.opExtrude","SWEPT_FACE",FACE,{"disambiguationData":[OSD([sQuery(id+"F2.wireOp",EDGE,"E107")])]}),makeQuery(id+"F3.opExtrude","SWEPT_FACE",FACE,{"disambiguationData":[OSD([sQuery(id+"F2.wireOp",EDGE,"E108")])]}),makeQuery(id+"F3.opExtrude","SWEPT_FACE",FACE,{"disambiguationData":[OSD([sQuery(id+"F2.wireOp",EDGE,"E109")])]})])],"derivedFrom":makeQuery(id+"F1.opExtrude","CAP_EDGE",EDGE,{"disambiguationData":[OSD([subQ0])],"isStart":false})});}
            var Q12;
            {var subQ0=sQuery(id+"F0.wireOp",EDGE,"E1");Q12=makeQuery(id+"F3.boolean.opBoolean","SPLIT",EDGE,{"disambiguationData":[TD([makeQuery(id+"F1.opExtrude","SWEPT_FACE",FACE,{"disambiguationData":[OSD([subQ0])]}),makeQuery(id+"F1.opExtrude","CAP_FACE",FACE,{"disambiguationData":[OSD([subQ0])],"isStart":false}),makeQuery(id+"F3.opExtrude","SWEPT_FACE",FACE,{"disambiguationData":[OSD([sQuery(id+"F2.wireOp",EDGE,"E104")])]}),makeQuery(id+"F3.opExtrude","SWEPT_FACE",FACE,{"disambiguationData":[OSD([sQuery(id+"F2.wireOp",EDGE,"E105")])]}),makeQuery(id+"F3.opExtrude","SWEPT_FACE",FACE,{"disambiguationData":[OSD([sQuery(id+"F2.wireOp",EDGE,"E106")])]}),makeQuery(id+"F3.opExtrude","SWEPT_FACE",FACE,{"disambiguationData":[OSD([sQuery(id+"F2.wireOp",EDGE,"E107")])]})])],"derivedFrom":makeQuery(id+"F1.opExtrude","CAP_EDGE",EDGE,{"disambiguationData":[OSD([subQ0])],"isStart":false})});}
            var Q13;
            {var subQ0=sQuery(id+"F0.wireOp",EDGE,"E1");Q13=makeQuery(id+"F3.boolean.opBoolean","SPLIT",EDGE,{"disambiguationData":[TD([makeQuery(id+"F1.opExtrude","SWEPT_FACE",FACE,{"disambiguationData":[OSD([subQ0])]}),makeQuery(id+"F1.opExtrude","CAP_FACE",FACE,{"disambiguationData":[OSD([subQ0])],"isStart":false}),makeQuery(id+"F3.opExtrude","SWEPT_FACE",FACE,{"disambiguationData":[OSD([sQuery(id+"F2.wireOp",EDGE,"E102")])]}),makeQuery(id+"F3.opExtrude","SWEPT_FACE",FACE,{"disambiguationData":[OSD([sQuery(id+"F2.wireOp",EDGE,"E103")])]}),makeQuery(id+"F3.opExtrude","SWEPT_FACE",FACE,{"disambiguationData":[OSD([sQuery(id+"F2.wireOp",EDGE,"E104")])]}),makeQuery(id+"F3.opExtrude","SWEPT_FACE",FACE,{"disambiguationData":[OSD([sQuery(id+"F2.wireOp",EDGE,"E105")])]})])],"derivedFrom":makeQuery(id+"F1.opExtrude","CAP_EDGE",EDGE,{"disambiguationData":[OSD([subQ0])],"isStart":false})});}
            var Q14;
            {var subQ0=sQuery(id+"F0.wireOp",EDGE,"E1");Q14=makeQuery(id+"F3.boolean.opBoolean","SPLIT",EDGE,{"disambiguationData":[TD([makeQuery(id+"F1.opExtrude","SWEPT_FACE",FACE,{"disambiguationData":[OSD([subQ0])]}),makeQuery(id+"F1.opExtrude","CAP_FACE",FACE,{"disambiguationData":[OSD([subQ0])],"isStart":false}),makeQuery(id+"F3.opExtrude","SWEPT_FACE",FACE,{"disambiguationData":[OSD([sQuery(id+"F2.wireOp",EDGE,"E100")])]}),makeQuery(id+"F3.opExtrude","SWEPT_FACE",FACE,{"disambiguationData":[OSD([sQuery(id+"F2.wireOp",EDGE,"E101")])]}),makeQuery(id+"F3.opExtrude","SWEPT_FACE",FACE,{"disambiguationData":[OSD([sQuery(id+"F2.wireOp",EDGE,"E102")])]}),makeQuery(id+"F3.opExtrude","SWEPT_FACE",FACE,{"disambiguationData":[OSD([sQuery(id+"F2.wireOp",EDGE,"E103")])]})])],"derivedFrom":makeQuery(id+"F1.opExtrude","CAP_EDGE",EDGE,{"disambiguationData":[OSD([subQ0])],"isStart":false})});}
            var Q15;
            {var subQ0=sQuery(id+"F0.wireOp",EDGE,"E1");Q15=makeQuery(id+"F3.boolean.opBoolean","SPLIT",EDGE,{"disambiguationData":[TD([makeQuery(id+"F1.opExtrude","SWEPT_FACE",FACE,{"disambiguationData":[OSD([subQ0])]}),makeQuery(id+"F1.opExtrude","CAP_FACE",FACE,{"disambiguationData":[OSD([subQ0])],"isStart":false}),makeQuery(id+"F3.opExtrude","SWEPT_FACE",FACE,{"disambiguationData":[OSD([sQuery(id+"F2.wireOp",EDGE,"E98")])]}),makeQuery(id+"F3.opExtrude","SWEPT_FACE",FACE,{"disambiguationData":[OSD([sQuery(id+"F2.wireOp",EDGE,"E99")])]}),makeQuery(id+"F3.opExtrude","SWEPT_FACE",FACE,{"disambiguationData":[OSD([sQuery(id+"F2.wireOp",EDGE,"E100")])]}),makeQuery(id+"F3.opExtrude","SWEPT_FACE",FACE,{"disambiguationData":[OSD([sQuery(id+"F2.wireOp",EDGE,"E101")])]})])],"derivedFrom":makeQuery(id+"F1.opExtrude","CAP_EDGE",EDGE,{"disambiguationData":[OSD([subQ0])],"isStart":false})});}
            var Q16;
            {var subQ0=sQuery(id+"F0.wireOp",EDGE,"E1");Q16=makeQuery(id+"F3.boolean.opBoolean","SPLIT",EDGE,{"disambiguationData":[TD([makeQuery(id+"F1.opExtrude","SWEPT_FACE",FACE,{"disambiguationData":[OSD([subQ0])]}),makeQuery(id+"F1.opExtrude","CAP_FACE",FACE,{"disambiguationData":[OSD([subQ0])],"isStart":false}),makeQuery(id+"F3.opExtrude","SWEPT_FACE",FACE,{"disambiguationData":[OSD([sQuery(id+"F2.wireOp",EDGE,"E96")])]}),makeQuery(id+"F3.opExtrude","SWEPT_FACE",FACE,{"disambiguationData":[OSD([sQuery(id+"F2.wireOp",EDGE,"E97")])]}),makeQuery(id+"F3.opExtrude","SWEPT_FACE",FACE,{"disambiguationData":[OSD([sQuery(id+"F2.wireOp",EDGE,"E98")])]}),makeQuery(id+"F3.opExtrude","SWEPT_FACE",FACE,{"disambiguationData":[OSD([sQuery(id+"F2.wireOp",EDGE,"E99")])]})])],"derivedFrom":makeQuery(id+"F1.opExtrude","CAP_EDGE",EDGE,{"disambiguationData":[OSD([subQ0])],"isStart":false})});}
            var Q17;
            {var subQ0=sQuery(id+"F0.wireOp",EDGE,"E1");Q17=makeQuery(id+"F3.boolean.opBoolean","SPLIT",EDGE,{"disambiguationData":[TD([makeQuery(id+"F1.opExtrude","SWEPT_FACE",FACE,{"disambiguationData":[OSD([subQ0])]}),makeQuery(id+"F1.opExtrude","CAP_FACE",FACE,{"disambiguationData":[OSD([subQ0])],"isStart":false}),makeQuery(id+"F3.opExtrude","SWEPT_FACE",FACE,{"disambiguationData":[OSD([sQuery(id+"F2.wireOp",EDGE,"E94")])]}),makeQuery(id+"F3.opExtrude","SWEPT_FACE",FACE,{"disambiguationData":[OSD([sQuery(id+"F2.wireOp",EDGE,"E95")])]}),makeQuery(id+"F3.opExtrude","SWEPT_FACE",FACE,{"disambiguationData":[OSD([sQuery(id+"F2.wireOp",EDGE,"E96")])]}),makeQuery(id+"F3.opExtrude","SWEPT_FACE",FACE,{"disambiguationData":[OSD([sQuery(id+"F2.wireOp",EDGE,"E97")])]})])],"derivedFrom":makeQuery(id+"F1.opExtrude","CAP_EDGE",EDGE,{"disambiguationData":[OSD([subQ0])],"isStart":false})});}
            var Q18;
            {var subQ0=sQuery(id+"F0.wireOp",EDGE,"E1");Q18=makeQuery(id+"F3.boolean.opBoolean","SPLIT",EDGE,{"disambiguationData":[TD([makeQuery(id+"F1.opExtrude","SWEPT_FACE",FACE,{"disambiguationData":[OSD([subQ0])]}),makeQuery(id+"F1.opExtrude","CAP_FACE",FACE,{"disambiguationData":[OSD([subQ0])],"isStart":false}),makeQuery(id+"F3.opExtrude","SWEPT_FACE",FACE,{"disambiguationData":[OSD([sQuery(id+"F2.wireOp",EDGE,"E92")])]}),makeQuery(id+"F3.opExtrude","SWEPT_FACE",FACE,{"disambiguationData":[OSD([sQuery(id+"F2.wireOp",EDGE,"E93")])]}),makeQuery(id+"F3.opExtrude","SWEPT_FACE",FACE,{"disambiguationData":[OSD([sQuery(id+"F2.wireOp",EDGE,"E94")])]}),makeQuery(id+"F3.opExtrude","SWEPT_FACE",FACE,{"disambiguationData":[OSD([sQuery(id+"F2.wireOp",EDGE,"E95")])]})])],"derivedFrom":makeQuery(id+"F1.opExtrude","CAP_EDGE",EDGE,{"disambiguationData":[OSD([subQ0])],"isStart":false})});}
            var Q19;
            {var subQ0=sQuery(id+"F0.wireOp",EDGE,"E1");Q19=makeQuery(id+"F3.boolean.opBoolean","SPLIT",EDGE,{"disambiguationData":[TD([makeQuery(id+"F1.opExtrude","SWEPT_FACE",FACE,{"disambiguationData":[OSD([subQ0])]}),makeQuery(id+"F1.opExtrude","CAP_FACE",FACE,{"disambiguationData":[OSD([subQ0])],"isStart":false}),makeQuery(id+"F3.opExtrude","SWEPT_FACE",FACE,{"disambiguationData":[OSD([sQuery(id+"F2.wireOp",EDGE,"E90")])]}),makeQuery(id+"F3.opExtrude","SWEPT_FACE",FACE,{"disambiguationData":[OSD([sQuery(id+"F2.wireOp",EDGE,"E91")])]}),makeQuery(id+"F3.opExtrude","SWEPT_FACE",FACE,{"disambiguationData":[OSD([sQuery(id+"F2.wireOp",EDGE,"E92")])]}),makeQuery(id+"F3.opExtrude","SWEPT_FACE",FACE,{"disambiguationData":[OSD([sQuery(id+"F2.wireOp",EDGE,"E93")])]})])],"derivedFrom":makeQuery(id+"F1.opExtrude","CAP_EDGE",EDGE,{"disambiguationData":[OSD([subQ0])],"isStart":false})});}
            var Q20;
            {var subQ0=sQuery(id+"F0.wireOp",EDGE,"E1");Q20=makeQuery(id+"F3.boolean.opBoolean","SPLIT",EDGE,{"disambiguationData":[TD([makeQuery(id+"F1.opExtrude","SWEPT_FACE",FACE,{"disambiguationData":[OSD([subQ0])]}),makeQuery(id+"F1.opExtrude","CAP_FACE",FACE,{"disambiguationData":[OSD([subQ0])],"isStart":false}),makeQuery(id+"F3.opExtrude","SWEPT_FACE",FACE,{"disambiguationData":[OSD([sQuery(id+"F2.wireOp",EDGE,"E88")])]}),makeQuery(id+"F3.opExtrude","SWEPT_FACE",FACE,{"disambiguationData":[OSD([sQuery(id+"F2.wireOp",EDGE,"E89")])]}),makeQuery(id+"F3.opExtrude","SWEPT_FACE",FACE,{"disambiguationData":[OSD([sQuery(id+"F2.wireOp",EDGE,"E90")])]}),makeQuery(id+"F3.opExtrude","SWEPT_FACE",FACE,{"disambiguationData":[OSD([sQuery(id+"F2.wireOp",EDGE,"E91")])]})])],"derivedFrom":makeQuery(id+"F1.opExtrude","CAP_EDGE",EDGE,{"disambiguationData":[OSD([subQ0])],"isStart":false})});}
            var Q21;
            {var subQ0=sQuery(id+"F0.wireOp",EDGE,"E1");Q21=makeQuery(id+"F3.boolean.opBoolean","SPLIT",EDGE,{"disambiguationData":[TD([makeQuery(id+"F1.opExtrude","SWEPT_FACE",FACE,{"disambiguationData":[OSD([subQ0])]}),makeQuery(id+"F1.opExtrude","CAP_FACE",FACE,{"disambiguationData":[OSD([subQ0])],"isStart":false}),makeQuery(id+"F3.opExtrude","SWEPT_FACE",FACE,{"disambiguationData":[OSD([sQuery(id+"F2.wireOp",EDGE,"E86")])]}),makeQuery(id+"F3.opExtrude","SWEPT_FACE",FACE,{"disambiguationData":[OSD([sQuery(id+"F2.wireOp",EDGE,"E87")])]}),makeQuery(id+"F3.opExtrude","SWEPT_FACE",FACE,{"disambiguationData":[OSD([sQuery(id+"F2.wireOp",EDGE,"E88")])]}),makeQuery(id+"F3.opExtrude","SWEPT_FACE",FACE,{"disambiguationData":[OSD([sQuery(id+"F2.wireOp",EDGE,"E89")])]})])],"derivedFrom":makeQuery(id+"F1.opExtrude","CAP_EDGE",EDGE,{"disambiguationData":[OSD([subQ0])],"isStart":false})});}
            var Q22;
            Q22=makeQuery(id+"F5.opExtrude","CAP_EDGE",EDGE,{"disambiguationData":[OSD([sQuery(id+"F4.wireOp",EDGE,"E117")])],"isStart":false});
            fillet(context, id + "F8", {"entities" : qUnion([Q0, Q1, Q2, Q3, Q4, Q5, Q6, Q7, Q8, Q9, Q10, Q11, Q12, Q13, Q14, Q15, Q16, Q17, Q18, Q19, Q20, Q21, Q22]), "radius" : 1.27 * mm, "tangentPropagation" : true, "allowEdgeOverflow" : false});
        }
    });
